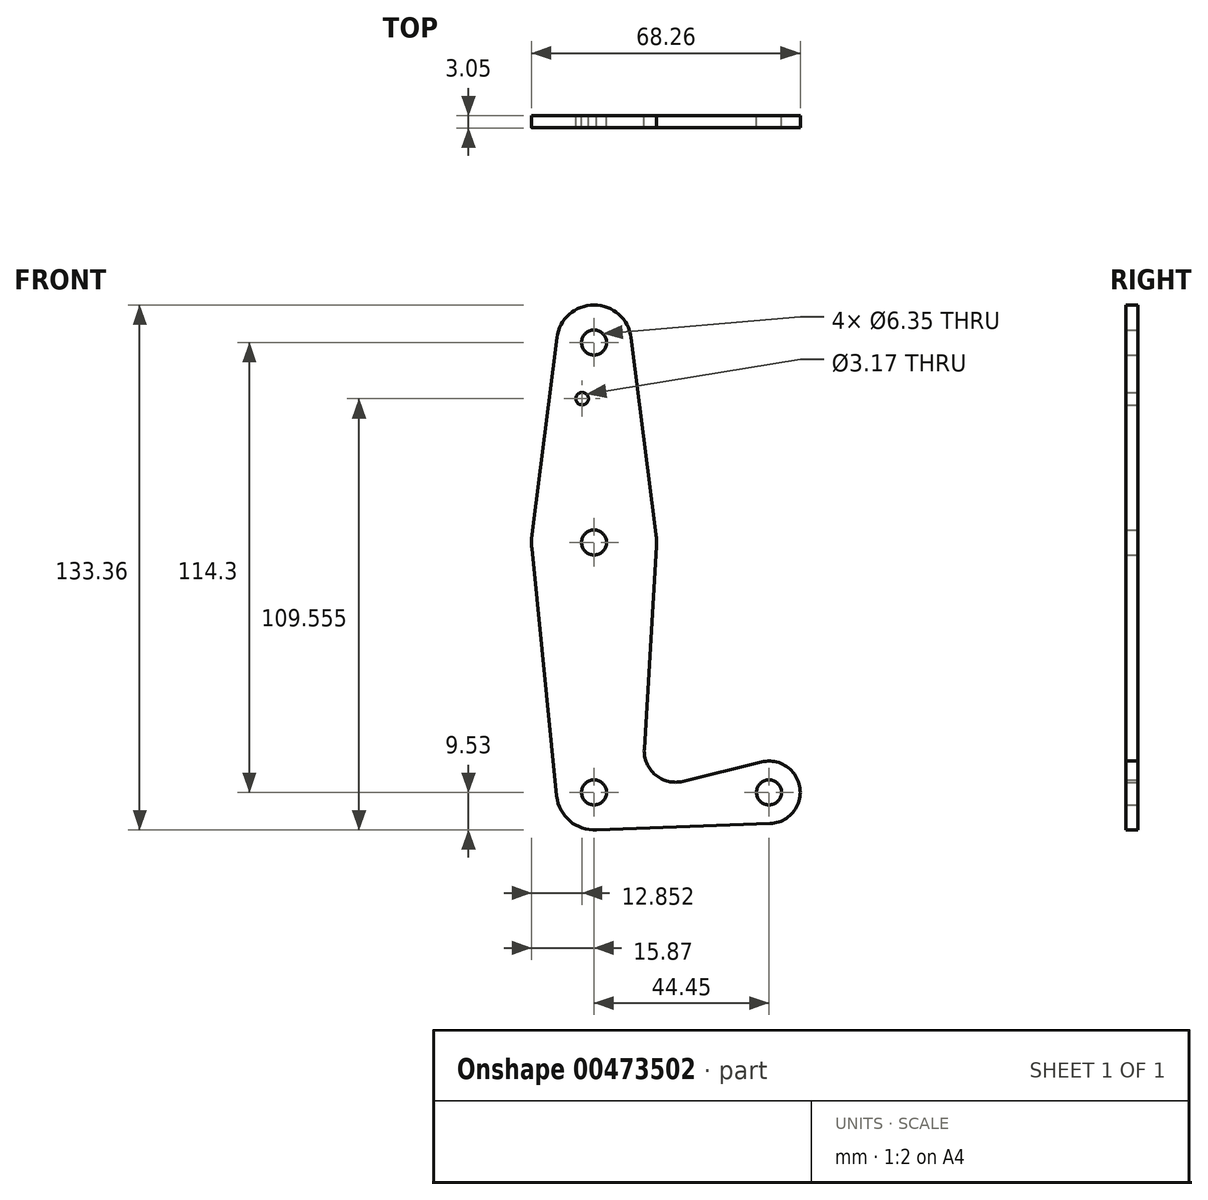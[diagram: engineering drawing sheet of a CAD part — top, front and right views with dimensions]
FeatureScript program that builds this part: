
annotation { "Feature Type Name" : "Feature", "Feature Type Description" : "" }
export const myFeature = defineFeature(function(context is Context, id is Id, definition is map)
    precondition{}
    {
        {
            var Q0;
            Q0=qCreatedBy(makeId("Front.planeOp"),FACE);
            var sketch = newSketch(context, id + "F0", { "sketchPlane" : qUnion([Q0])});
            skLineSegment(sketch, "E0", {"start": v(0, 0) * mm, "end": v(44.45, 0) * mm, "construction": true});
            skLineSegment(sketch, "E1", {"start": v(0, 0) * mm, "end": v(0, 114.3) * mm, "construction": true});
            skCircle(sketch, "E2", {"center": v(0, 114.3) * mm, "radius": 9.53 * mm});
            skCircle(sketch, "E3", {"center": v(0, 63.5) * mm, "radius": 15.88 * mm});
            skCircle(sketch, "E4", {"center": v(0, 0) * mm, "radius": 9.53 * mm});
            skCircle(sketch, "E5", {"center": v(44.45, 0) * mm, "radius": 7.94 * mm});
            skLineSegment(sketch, "E6", {"start": v(-9.45, 115.5) * mm, "end": v(-15.75, 65.48) * mm});
            skLineSegment(sketch, "E7", {"start": v(9.45, 115.5) * mm, "end": v(15.75, 65.48) * mm});
            skLineSegment(sketch, "E8", {"start": v(15.85, 62.55) * mm, "end": v(12.76, 11) * mm});
            skLineSegment(sketch, "E9", {"start": v(22.6, 2.8) * mm, "end": v(42.56, 7.7) * mm});
            skLineSegment(sketch, "E10", {"start": v(0, -9.53) * mm, "end": v(44.73, -7.93) * mm});
            skCircle(sketch, "E11", {"center": v(0, 114.3) * mm, "radius": 3.18 * mm});
            skCircle(sketch, "E12", {"center": v(-3.02, 100.03) * mm, "radius": 1.59 * mm});
            skCircle(sketch, "E13", {"center": v(0, 63.5) * mm, "radius": 3.18 * mm});
            skCircle(sketch, "E14", {"center": v(0, 0) * mm, "radius": 3.18 * mm});
            skCircle(sketch, "E15", {"center": v(44.45, 0) * mm, "radius": 3.18 * mm});
            skArc(sketch, "E16.filletArc", {"start": v(12.76, 11) * mm, "mid": v(15.6, 4.42) * mm, "end": v(22.6, 2.8) * mm});
            skLineSegment(sketch, "E17", {"start": v(-15.8, 61.91) * mm, "end": v(-9.48, -0.95) * mm});
            skSolve(sketch);
        }
        {
            var Q0;
            Q0 = qSketchRegion(id + "F0", true);
            extrude(context, id + "F1", {"entities" : qUnion([Q0]), "depth" : 3.05 * mm});
        }
    });
